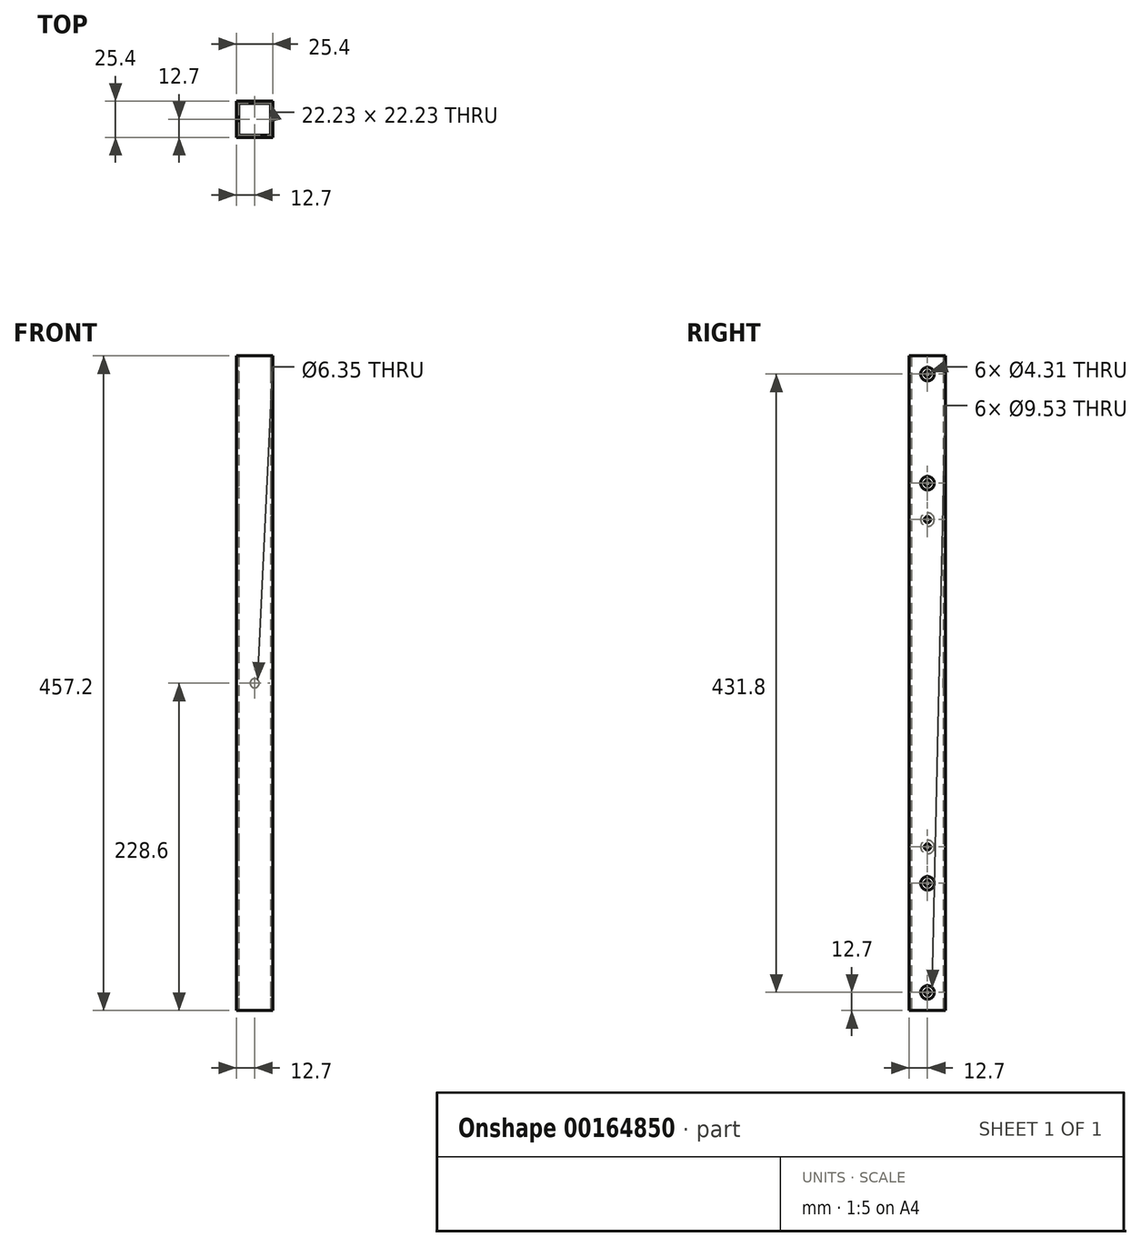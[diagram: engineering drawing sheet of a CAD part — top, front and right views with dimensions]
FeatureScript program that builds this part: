
annotation { "Feature Type Name" : "Feature", "Feature Type Description" : "" }
export const myFeature = defineFeature(function(context is Context, id is Id, definition is map)
    precondition{}
    {
        {
            var Q0;
            Q0=qCreatedBy(makeId("Top.planeOp"),FACE);
            var sketch = newSketch(context, id + "F0", { "sketchPlane" : qUnion([Q0])});
            skLineSegment(sketch, "E0.bottom", {"start": v(11.11, -11.11) * mm, "end": v(-11.11, -11.11) * mm});
            skLineSegment(sketch, "E0.top", {"start": v(11.11, 11.11) * mm, "end": v(-11.11, 11.11) * mm});
            skLineSegment(sketch, "E0.left", {"start": v(11.11, -11.11) * mm, "end": v(11.11, 11.11) * mm});
            skLineSegment(sketch, "E0.right", {"start": v(-11.11, -11.11) * mm, "end": v(-11.11, 11.11) * mm});
            skPoint(sketch, "E0.middle", {"position": v(0, 0) * mm});
            skLineSegment(sketch, "E1.bottom", {"start": v(12.7, -12.7) * mm, "end": v(-12.7, -12.7) * mm});
            skLineSegment(sketch, "E1.top", {"start": v(12.7, 12.7) * mm, "end": v(-12.7, 12.7) * mm});
            skLineSegment(sketch, "E1.left", {"start": v(12.7, -12.7) * mm, "end": v(12.7, 12.7) * mm});
            skLineSegment(sketch, "E1.right", {"start": v(-12.7, -12.7) * mm, "end": v(-12.7, 12.7) * mm});
            skSolve(sketch);
        }
        {
            var Q0;
            Q0=qSketchRegion(id+"F0",true);
            extrude(context, id + "F1", {"entities" : qUnion([Q0]), "depth" : 457.2 * mm});
        }
        {
            var Q0;
            Q0=makeQuery(id+"F1.opExtrude","SWEPT_FACE",FACE,{"disambiguationData":[OSD([sQuery(id+"F0.wireOp",EDGE,"E1.top")])]});
            var sketch = newSketch(context, id + "F2", { "sketchPlane" : qUnion([Q0])});
            skLineSegment(sketch, "E2", {"start": v(12.7, 228.6) * mm, "end": v(-12.7, 228.6) * mm, "construction": true});
            skCircle(sketch, "E3", {"center": v(0, 228.6) * mm, "radius": 3.17 * mm});
            skSolve(sketch);
        }
        {
            var Q0;
            Q0=qSketchRegion(id+"F2",true);
            var Q1;
            Q1=makeQuery(id+"F1.opExtrude","SWEPT_FACE",FACE,{"disambiguationData":[OSD([sQuery(id+"F0.wireOp",EDGE,"E0.top")])]});
            extrude(context, id + "F3", {"entities" : qUnion([Q0]), "operationType" : NewBodyOperationType.REMOVE, "endBound" : BoundingType.UP_TO_SURFACE, "oppositeDirection" : true, "endBoundEntityFace" : qUnion([Q1]), "depth" : 25.4 * mm});
        }
        {
            var Q0;
            Q0=makeQuery(id+"F1.opExtrude","SWEPT_FACE",FACE,{"disambiguationData":[OSD([sQuery(id+"F0.wireOp",EDGE,"E1.right")])]});
            var sketch = newSketch(context, id + "F4", { "sketchPlane" : qUnion([Q0])});
            skLineSegment(sketch, "E4.bottom", {"start": v(0, 0) * mm, "end": v(-12.7, 0) * mm, "construction": true});
            skLineSegment(sketch, "E4.top", {"start": v(0, 12.7) * mm, "end": v(-12.7, 12.7) * mm, "construction": true});
            skLineSegment(sketch, "E4.left", {"start": v(0, 0) * mm, "end": v(0, 12.7) * mm, "construction": true});
            skLineSegment(sketch, "E4.right", {"start": v(-12.7, 0) * mm, "end": v(-12.7, 12.7) * mm, "construction": true});
            skLineSegment(sketch, "E5.bottom", {"start": v(0, 457.2) * mm, "end": v(-12.7, 457.2) * mm, "construction": true});
            skLineSegment(sketch, "E5.top", {"start": v(0, 444.5) * mm, "end": v(-12.7, 444.5) * mm, "construction": true});
            skLineSegment(sketch, "E5.left", {"start": v(0, 457.2) * mm, "end": v(0, 444.5) * mm, "construction": true});
            skLineSegment(sketch, "E5.right", {"start": v(-12.7, 457.2) * mm, "end": v(-12.7, 444.5) * mm, "construction": true});
            skLineSegment(sketch, "E6", {"start": v(0, 12.7) * mm, "end": v(0, 88.9) * mm, "construction": true});
            skLineSegment(sketch, "E7", {"start": v(0, 444.5) * mm, "end": v(0, 368.3) * mm, "construction": true});
            skCircle(sketch, "E8", {"center": v(0, 12.7) * mm, "radius": 2.15 * mm});
            skCircle(sketch, "E9", {"center": v(0, 88.9) * mm, "radius": 2.15 * mm});
            skCircle(sketch, "E10", {"center": v(0, 444.5) * mm, "radius": 2.15 * mm});
            skCircle(sketch, "E11", {"center": v(0, 368.3) * mm, "radius": 2.15 * mm});
            skLineSegment(sketch, "E12", {"start": v(0, 368.3) * mm, "end": v(0, 342.9) * mm, "construction": true});
            skLineSegment(sketch, "E13", {"start": v(0, 342.9) * mm, "end": v(0, 114.3) * mm, "construction": true});
            skLineSegment(sketch, "E14", {"start": v(0, 114.3) * mm, "end": v(0, 88.9) * mm, "construction": true});
            skCircle(sketch, "E15", {"center": v(0, 342.9) * mm, "radius": 2.15 * mm});
            skCircle(sketch, "E16", {"center": v(0, 114.3) * mm, "radius": 2.15 * mm});
            skSolve(sketch);
        }
        {
            var Q0;
            Q0=qSketchRegion(id+"F4",true);
            var Q1;
            Q1=makeQuery(id+"F1.opExtrude","SWEPT_FACE",FACE,{"disambiguationData":[OSD([sQuery(id+"F0.wireOp",EDGE,"E1.left")])]});
            extrude(context, id + "F5", {"entities" : qUnion([Q0]), "operationType" : NewBodyOperationType.REMOVE, "endBound" : BoundingType.UP_TO_SURFACE, "oppositeDirection" : true, "endBoundEntityFace" : qUnion([Q1]), "depth" : 25.4 * mm});
        }
        {
            var Q0;
            Q0=makeQuery(id+"F1.opExtrude","SWEPT_FACE",FACE,{"disambiguationData":[OSD([sQuery(id+"F0.wireOp",EDGE,"E1.left")])]});
            var sketch = newSketch(context, id + "F6", { "sketchPlane" : qUnion([Q0])});
            skCircle(sketch, "E17", {"center": v(0, 444.5) * mm, "radius": 4.76 * mm});
            skCircle(sketch, "E18", {"center": v(0, 368.3) * mm, "radius": 4.76 * mm});
            skCircle(sketch, "E19", {"center": v(0, 12.7) * mm, "radius": 4.76 * mm});
            skCircle(sketch, "E20", {"center": v(0, 88.9) * mm, "radius": 4.76 * mm});
            skSolve(sketch);
        }
        {
            var Q0;
            Q0 = qSketchRegion(id + "F6", true);
            var Q1;
            Q1=makeQuery(id+"F1.opExtrude","SWEPT_FACE",FACE,{"disambiguationData":[OSD([sQuery(id+"F0.wireOp",EDGE,"E0.left")])]});
            extrude(context, id + "F7", {"entities" : qUnion([Q0]), "operationType" : NewBodyOperationType.REMOVE, "endBound" : BoundingType.UP_TO_SURFACE, "oppositeDirection" : true, "endBoundEntityFace" : qUnion([Q1]), "depth" : 25.4 * mm});
        }
        {
            var Q0;
            Q0=makeQuery(id+"F1.opExtrude","SWEPT_FACE",FACE,{"disambiguationData":[OSD([sQuery(id+"F0.wireOp",EDGE,"E1.right")])]});
            var sketch = newSketch(context, id + "F8", { "sketchPlane" : qUnion([Q0])});
            skCircle(sketch, "E21", {"center": v(0, 342.9) * mm, "radius": 4.76 * mm});
            skCircle(sketch, "E22", {"center": v(0, 114.3) * mm, "radius": 4.76 * mm});
            skSolve(sketch);
        }
        {
            var Q0;
            Q0 = qSketchRegion(id + "F8", true);
            var Q1;
            Q1=makeQuery(id+"F1.opExtrude","SWEPT_FACE",FACE,{"disambiguationData":[OSD([sQuery(id+"F0.wireOp",EDGE,"E0.right")])]});
            extrude(context, id + "F9", {"entities" : qUnion([Q0]), "operationType" : NewBodyOperationType.REMOVE, "endBound" : BoundingType.UP_TO_SURFACE, "oppositeDirection" : true, "endBoundEntityFace" : qUnion([Q1]), "depth" : 25.4 * mm});
        }
    });
